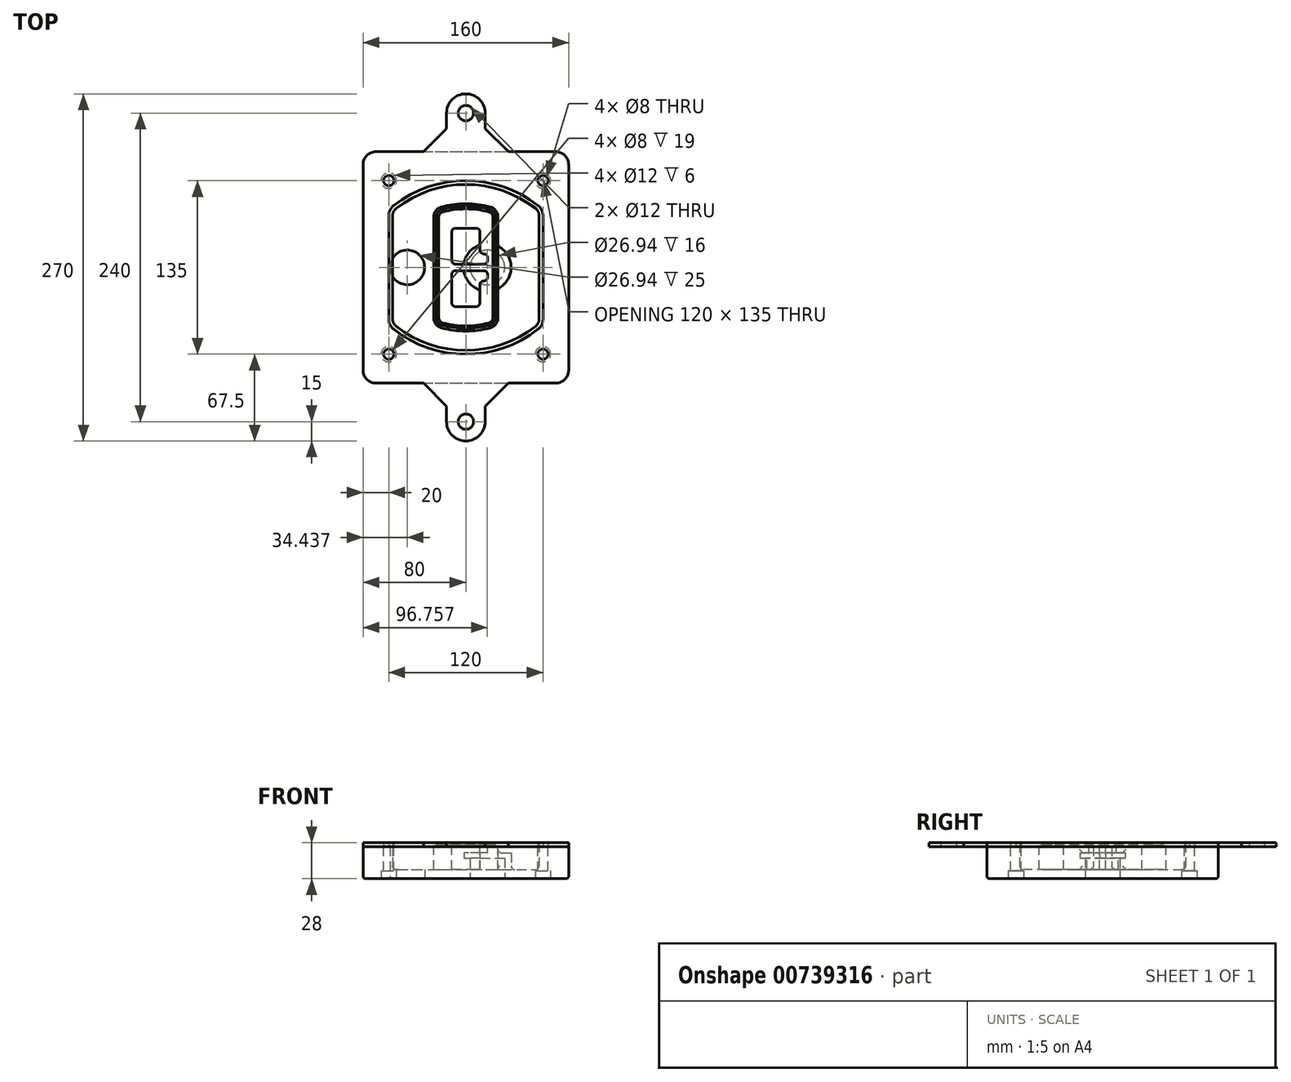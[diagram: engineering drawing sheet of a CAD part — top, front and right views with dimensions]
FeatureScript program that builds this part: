
annotation { "Feature Type Name" : "Feature", "Feature Type Description" : "" }
export const myFeature = defineFeature(function(context is Context, id is Id, definition is map)
    precondition{}
    {
        {
            var Q0;
            Q0=qCreatedBy(makeId("Top.planeOp"),FACE);
            var sketch = newSketch(context, id + "F0", { "sketchPlane" : qUnion([Q0])});
            skPoint(sketch, "E0.rect.middle", {"position": v(0, 0) * mm});
            skLineSegment(sketch, "E1.bottom", {"start": v(-70, -90) * mm, "end": v(70, -90) * mm});
            skLineSegment(sketch, "E1.top", {"start": v(-70, 90) * mm, "end": v(70, 90) * mm});
            skLineSegment(sketch, "E1.left", {"start": v(-80, -80) * mm, "end": v(-80, 80) * mm});
            skLineSegment(sketch, "E1.right", {"start": v(80, -80) * mm, "end": v(80, 80) * mm});
            skLineSegment(sketch, "E2", {"start": v(-80, 90) * mm, "end": v(80, -90) * mm, "construction": true});
            skLineSegment(sketch, "E3", {"start": v(80, 90) * mm, "end": v(-80, -90) * mm, "construction": true});
            skCircle(sketch, "E4", {"center": v(-60, 67.5) * mm, "radius": 4 * mm});
            skCircle(sketch, "E5", {"center": v(60, 67.5) * mm, "radius": 4 * mm});
            skCircle(sketch, "E6", {"center": v(60, -67.5) * mm, "radius": 4 * mm});
            skCircle(sketch, "E7", {"center": v(-60, -67.5) * mm, "radius": 4 * mm});
            skLineSegment(sketch, "E8", {"start": v(-60, 67.5) * mm, "end": v(60, 67.5) * mm, "construction": true});
            skLineSegment(sketch, "E9", {"start": v(60, 67.5) * mm, "end": v(60, -67.5) * mm, "construction": true});
            skLineSegment(sketch, "E10", {"start": v(60, -67.5) * mm, "end": v(-60, -67.5) * mm, "construction": true});
            skLineSegment(sketch, "E11", {"start": v(-60, -67.5) * mm, "end": v(-60, 67.5) * mm, "construction": true});
            skLineSegment(sketch, "E12", {"start": v(-60, 40.3) * mm, "end": v(-60, -40.3) * mm});
            skLineSegment(sketch, "E13", {"start": v(60, 40.3) * mm, "end": v(60, -40.3) * mm});
            skArc(sketch, "E14", {"start": v(56.15, 48.18) * mm, "mid": v(0, 67.5) * mm, "end": v(-56.15, 48.18) * mm});
            skArc(sketch, "E15", {"start": v(-56.15, -48.18) * mm, "mid": v(0, -67.5) * mm, "end": v(56.15, -48.18) * mm});
            skLineSegment(sketch, "E16", {"start": v(-60, 0) * mm, "end": v(60, 0) * mm, "construction": true});
            skPoint(sketch, "E17.visualSharp", {"position": v(-60, -45) * mm});
            skArc(sketch, "E17.filletArc", {"start": v(-60, -40.3) * mm, "mid": v(-58.99, -44.68) * mm, "end": v(-56.15, -48.18) * mm});
            skPoint(sketch, "E18.visualSharp", {"position": v(-60, 45) * mm});
            skArc(sketch, "E18.filletArc", {"start": v(-56.15, 48.18) * mm, "mid": v(-58.99, 44.68) * mm, "end": v(-60, 40.3) * mm});
            skPoint(sketch, "E19.visualSharp", {"position": v(60, 45) * mm});
            skArc(sketch, "E19.filletArc", {"start": v(60, 40.3) * mm, "mid": v(58.99, 44.68) * mm, "end": v(56.15, 48.18) * mm});
            skPoint(sketch, "E20.visualSharp", {"position": v(60, -45) * mm});
            skArc(sketch, "E20.filletArc", {"start": v(56.15, -48.18) * mm, "mid": v(58.99, -44.68) * mm, "end": v(60, -40.3) * mm});
            skPoint(sketch, "E21.visualSharp", {"position": v(-80, 90) * mm});
            skArc(sketch, "E21.filletArc", {"start": v(-70, 90) * mm, "mid": v(-77.07, 87.07) * mm, "end": v(-80, 80) * mm});
            skPoint(sketch, "E22.visualSharp", {"position": v(80, 90) * mm});
            skArc(sketch, "E22.filletArc", {"start": v(80, 80) * mm, "mid": v(77.07, 87.07) * mm, "end": v(70, 90) * mm});
            skPoint(sketch, "E23.visualSharp", {"position": v(80, -90) * mm});
            skArc(sketch, "E23.filletArc", {"start": v(70, -90) * mm, "mid": v(77.07, -87.07) * mm, "end": v(80, -80) * mm});
            skPoint(sketch, "E24.visualSharp", {"position": v(-80, -90) * mm});
            skArc(sketch, "E24.filletArc", {"start": v(-80, -80) * mm, "mid": v(-77.07, -87.07) * mm, "end": v(-70, -90) * mm});
            skArc(sketch, "E25.0", {"start": v(57, 40.3) * mm, "mid": v(56.3, 43.36) * mm, "end": v(54.3, 45.81) * mm});
            skLineSegment(sketch, "E25.1", {"start": v(57, 40.3) * mm, "end": v(57, -40.3) * mm});
            skArc(sketch, "E25.2", {"start": v(54.3, -45.81) * mm, "mid": v(56.3, -43.36) * mm, "end": v(57, -40.3) * mm});
            skArc(sketch, "E25.3", {"start": v(-54.3, -45.81) * mm, "mid": v(0, -64.5) * mm, "end": v(54.3, -45.81) * mm});
            skArc(sketch, "E25.4", {"start": v(-57, -40.3) * mm, "mid": v(-56.3, -43.36) * mm, "end": v(-54.3, -45.81) * mm});
            skArc(sketch, "E25.5", {"start": v(54.3, 45.81) * mm, "mid": v(0, 64.5) * mm, "end": v(-54.3, 45.81) * mm});
            skLineSegment(sketch, "E25.6", {"start": v(-57, 40.3) * mm, "end": v(-57, -40.3) * mm});
            skArc(sketch, "E25.7", {"start": v(-54.3, 45.81) * mm, "mid": v(-56.3, 43.36) * mm, "end": v(-57, 40.3) * mm});
            skArc(sketch, "E26.0", {"start": v(-58.62, 51.33) * mm, "mid": v(-62.58, 46.43) * mm, "end": v(-64, 40.3) * mm});
            skArc(sketch, "E26.1", {"start": v(58.62, 51.33) * mm, "mid": v(0, 71.5) * mm, "end": v(-58.62, 51.33) * mm});
            skArc(sketch, "E26.2", {"start": v(64, 40.3) * mm, "mid": v(62.58, 46.43) * mm, "end": v(58.62, 51.33) * mm});
            skLineSegment(sketch, "E26.3", {"start": v(64, 40.3) * mm, "end": v(64, -40.3) * mm});
            skArc(sketch, "E26.4", {"start": v(58.62, -51.33) * mm, "mid": v(62.58, -46.43) * mm, "end": v(64, -40.3) * mm});
            skLineSegment(sketch, "E26.5", {"start": v(-64, 40.3) * mm, "end": v(-64, -40.3) * mm});
            skArc(sketch, "E26.6", {"start": v(-58.62, -51.33) * mm, "mid": v(0, -71.5) * mm, "end": v(58.62, -51.33) * mm});
            skArc(sketch, "E26.7", {"start": v(-64, -40.3) * mm, "mid": v(-62.58, -46.43) * mm, "end": v(-58.62, -51.33) * mm});
            skSolve(sketch);
        }
        {
            var Q0;
            Q0=makeQuery(id+"F0.imprint","IMPRINT",FACE,{"disambiguationData":[TD([[makeQuery(id+"F0.imprint","IMPRINT",EDGE,{"derivedFrom":sQuery(id+"F0.wireOp",EDGE,"E1.bottom")}),1.0]])]});
            var Q1;
            Q1=makeQuery(id+"F0.imprint","IMPRINT",FACE,{"disambiguationData":[TD([[makeQuery(id+"F0.imprint","IMPRINT",EDGE,{"derivedFrom":sQuery(id+"F0.wireOp",EDGE,"E12")}),1.0]])]});
            var Q2;
            Q2=makeQuery(id+"F0.imprint","IMPRINT",FACE,{"disambiguationData":[TD([[makeQuery(id+"F0.imprint","IMPRINT",EDGE,{"derivedFrom":sQuery(id+"F0.wireOp",EDGE,"E25.0")}),1.0]])]});
            var Q3;
            Q3=makeQuery(id+"F0.imprint","IMPRINT",FACE,{"disambiguationData":[TD([[makeQuery(id+"F0.imprint","IMPRINT",EDGE,{"derivedFrom":sQuery(id+"F0.wireOp",EDGE,"E12")}),-1.0]])]});
            extrude(context, id + "F1", {"entities" : qUnion([Q0, Q1, Q2, Q3]), "oppositeDirection" : true, "depth" : 25 * mm});
        }
        {
            var Q0;
            Q0=makeQuery(id+"F0.imprint","IMPRINT",FACE,{"disambiguationData":[TD([[makeQuery(id+"F0.imprint","IMPRINT",EDGE,{"derivedFrom":sQuery(id+"F0.wireOp",EDGE,"E12")}),1.0]])]});
            extrude(context, id + "F2", {"entities" : qUnion([Q0]), "operationType" : NewBodyOperationType.ADD, "depth" : 3 * mm, "offsetDistance" : 25 * mm});
        }
        {
            var Q0;
            Q0=makeQuery(id+"F0.imprint","IMPRINT",FACE,{"disambiguationData":[TD([[makeQuery(id+"F0.imprint","IMPRINT",EDGE,{"derivedFrom":sQuery(id+"F0.wireOp",EDGE,"E25.0")}),1.0]])]});
            extrude(context, id + "F3", {"entities" : qUnion([Q0]), "operationType" : NewBodyOperationType.REMOVE, "oppositeDirection" : true, "depth" : 18 * mm});
        }
        {
            var Q0;
            Q0=makeQuery(id+"F2.opExtrude","CAP_FACE",FACE,{"disambiguationData":[OSD([sQuery(id+"F0.wireOp",EDGE,"E12"),sQuery(id+"F0.wireOp",EDGE,"E13"),sQuery(id+"F0.wireOp",EDGE,"E14"),sQuery(id+"F0.wireOp",EDGE,"E15"),sQuery(id+"F0.wireOp",EDGE,"E17.filletArc"),sQuery(id+"F0.wireOp",EDGE,"E18.filletArc"),sQuery(id+"F0.wireOp",EDGE,"E19.filletArc"),sQuery(id+"F0.wireOp",EDGE,"E20.filletArc"),sQuery(id+"F0.wireOp",EDGE,"E25.0"),sQuery(id+"F0.wireOp",EDGE,"E25.1"),sQuery(id+"F0.wireOp",EDGE,"E25.2"),sQuery(id+"F0.wireOp",EDGE,"E25.3"),sQuery(id+"F0.wireOp",EDGE,"E25.4"),sQuery(id+"F0.wireOp",EDGE,"E25.5"),sQuery(id+"F0.wireOp",EDGE,"E25.6"),sQuery(id+"F0.wireOp",EDGE,"E25.7")])],"isStart":false});
            var sketch = newSketch(context, id + "F4", { "sketchPlane" : qUnion([Q0])});
            skArc(sketch, "E27.0", {"start": v(-19.08, -46.97) * mm, "mid": v(0, -49.5) * mm, "end": v(19.08, -46.97) * mm});
            skArc(sketch, "E28.0", {"start": v(19.08, 46.97) * mm, "mid": v(0, 49.5) * mm, "end": v(-19.08, 46.97) * mm});
            skLineSegment(sketch, "E29", {"start": v(-25, 39.25) * mm, "end": v(-25, -39.25) * mm});
            skLineSegment(sketch, "E30", {"start": v(25, 39.25) * mm, "end": v(25, -39.25) * mm});
            skLineSegment(sketch, "E31", {"start": v(-25, 45.1) * mm, "end": v(25, 45.1) * mm, "construction": true});
            skLineSegment(sketch, "E32", {"start": v(-25, -45.1) * mm, "end": v(25, -45.1) * mm, "construction": true});
            skPoint(sketch, "E33.visualSharp", {"position": v(-25, 45.1) * mm});
            skArc(sketch, "E33.filletArc", {"start": v(-19.08, 46.97) * mm, "mid": v(-23.35, 44.11) * mm, "end": v(-25, 39.25) * mm});
            skPoint(sketch, "E34.visualSharp", {"position": v(25, 45.1) * mm});
            skArc(sketch, "E34.filletArc", {"start": v(25, 39.25) * mm, "mid": v(23.35, 44.11) * mm, "end": v(19.08, 46.97) * mm});
            skPoint(sketch, "E35.visualSharp", {"position": v(25, -45.1) * mm});
            skArc(sketch, "E35.filletArc", {"start": v(19.08, -46.97) * mm, "mid": v(23.35, -44.11) * mm, "end": v(25, -39.25) * mm});
            skPoint(sketch, "E36.visualSharp", {"position": v(-25, -45.1) * mm});
            skArc(sketch, "E36.filletArc", {"start": v(-25, -39.25) * mm, "mid": v(-23.35, -44.11) * mm, "end": v(-19.08, -46.97) * mm});
            skArc(sketch, "E37.0", {"start": v(54.3, 45.81) * mm, "mid": v(0, 64.5) * mm, "end": v(-54.3, 45.81) * mm});
            skArc(sketch, "E37.1", {"start": v(-54.3, 45.81) * mm, "mid": v(-56.3, 43.36) * mm, "end": v(-57, 40.3) * mm});
            skLineSegment(sketch, "E37.2", {"start": v(-57, 40.3) * mm, "end": v(-57, -40.3) * mm});
            skArc(sketch, "E37.3", {"start": v(-57, -40.3) * mm, "mid": v(-56.3, -43.36) * mm, "end": v(-54.3, -45.81) * mm});
            skArc(sketch, "E37.4", {"start": v(-54.3, -45.81) * mm, "mid": v(0, -64.5) * mm, "end": v(54.3, -45.81) * mm});
            skArc(sketch, "E37.5", {"start": v(54.3, -45.81) * mm, "mid": v(56.3, -43.36) * mm, "end": v(57, -40.3) * mm});
            skLineSegment(sketch, "E37.6", {"start": v(57, 40.3) * mm, "end": v(57, -40.3) * mm});
            skArc(sketch, "E37.7", {"start": v(57, 40.3) * mm, "mid": v(56.3, 43.36) * mm, "end": v(54.3, 45.81) * mm});
            skLineSegment(sketch, "E38.0", {"start": v(23, 39.25) * mm, "end": v(23, -39.25) * mm});
            skArc(sketch, "E38.1", {"start": v(18.56, -45.04) * mm, "mid": v(21.76, -42.9) * mm, "end": v(23, -39.25) * mm});
            skArc(sketch, "E38.2", {"start": v(-18.56, -45.04) * mm, "mid": v(0, -47.5) * mm, "end": v(18.56, -45.04) * mm});
            skArc(sketch, "E38.3", {"start": v(-23, -39.25) * mm, "mid": v(-21.76, -42.9) * mm, "end": v(-18.56, -45.04) * mm});
            skLineSegment(sketch, "E38.4", {"start": v(-23, 39.25) * mm, "end": v(-23, -39.25) * mm});
            skArc(sketch, "E38.5", {"start": v(23, 39.25) * mm, "mid": v(21.76, 42.9) * mm, "end": v(18.56, 45.04) * mm});
            skArc(sketch, "E38.6", {"start": v(-18.56, 45.04) * mm, "mid": v(-21.76, 42.9) * mm, "end": v(-23, 39.25) * mm});
            skArc(sketch, "E38.7", {"start": v(18.56, 45.04) * mm, "mid": v(0, 47.5) * mm, "end": v(-18.56, 45.04) * mm});
            skArc(sketch, "E39.0", {"start": v(21, 39.25) * mm, "mid": v(20.18, 41.68) * mm, "end": v(18.04, 43.1) * mm});
            skLineSegment(sketch, "E39.1", {"start": v(21, 39.25) * mm, "end": v(21, -39.25) * mm});
            skArc(sketch, "E39.2", {"start": v(18.04, -43.1) * mm, "mid": v(20.18, -41.68) * mm, "end": v(21, -39.25) * mm});
            skArc(sketch, "E39.3", {"start": v(-18.04, -43.1) * mm, "mid": v(0, -45.5) * mm, "end": v(18.04, -43.1) * mm});
            skArc(sketch, "E39.4", {"start": v(-21, -39.25) * mm, "mid": v(-20.18, -41.68) * mm, "end": v(-18.04, -43.1) * mm});
            skArc(sketch, "E39.5", {"start": v(18.04, 43.1) * mm, "mid": v(0, 45.5) * mm, "end": v(-18.04, 43.1) * mm});
            skLineSegment(sketch, "E39.6", {"start": v(-21, 39.25) * mm, "end": v(-21, -39.25) * mm});
            skArc(sketch, "E39.7", {"start": v(-18.04, 43.1) * mm, "mid": v(-20.18, 41.68) * mm, "end": v(-21, 39.25) * mm});
            skLineSegment(sketch, "E40", {"start": v(-25, 0) * mm, "end": v(25, 0) * mm, "construction": true});
            skLineSegment(sketch, "E41", {"start": v(-11, 5.5) * mm, "end": v(-11, 27.5) * mm});
            skLineSegment(sketch, "E42", {"start": v(-8, 30.5) * mm, "end": v(8, 30.5) * mm});
            skLineSegment(sketch, "E43", {"start": v(11, 27.5) * mm, "end": v(11, 13.5) * mm});
            skLineSegment(sketch, "E44", {"start": v(14, 10.5) * mm, "end": v(14, 10.5) * mm});
            skLineSegment(sketch, "E45", {"start": v(17, 7.5) * mm, "end": v(17, 5.5) * mm});
            skLineSegment(sketch, "E46", {"start": v(14, 2.5) * mm, "end": v(-8, 2.5) * mm});
            skPoint(sketch, "E47.visualSharp", {"position": v(-11, 30.5) * mm});
            skArc(sketch, "E47.filletArc", {"start": v(-8, 30.5) * mm, "mid": v(-10.12, 29.62) * mm, "end": v(-11, 27.5) * mm});
            skPoint(sketch, "E48.visualSharp", {"position": v(11, 30.5) * mm});
            skArc(sketch, "E48.filletArc", {"start": v(11, 27.5) * mm, "mid": v(10.12, 29.62) * mm, "end": v(8, 30.5) * mm});
            skPoint(sketch, "E49.visualSharp", {"position": v(11, 10.5) * mm});
            skArc(sketch, "E49.filletArc", {"start": v(11, 13.5) * mm, "mid": v(11.88, 11.38) * mm, "end": v(14, 10.5) * mm});
            skPoint(sketch, "E50.visualSharp", {"position": v(17, 10.5) * mm});
            skArc(sketch, "E50.filletArc", {"start": v(17, 7.5) * mm, "mid": v(16.12, 9.62) * mm, "end": v(14, 10.5) * mm});
            skPoint(sketch, "E51.visualSharp", {"position": v(17, 2.5) * mm});
            skArc(sketch, "E51.filletArc", {"start": v(14, 2.5) * mm, "mid": v(16.12, 3.38) * mm, "end": v(17, 5.5) * mm});
            skPoint(sketch, "E52.visualSharp", {"position": v(-11, 2.5) * mm});
            skArc(sketch, "E52.filletArc", {"start": v(-11, 5.5) * mm, "mid": v(-10.12, 3.38) * mm, "end": v(-8, 2.5) * mm});
            skLineSegment(sketch, "E53.0.MirrorCS", {"start": v(14, -2.5) * mm, "end": v(-8, -2.5) * mm});
            skArc(sketch, "E54.0.MirrorCS", {"start": v(-11, -5.5) * mm, "mid": v(-10.12, -3.38) * mm, "end": v(-8, -2.5) * mm});
            skLineSegment(sketch, "E55.0.MirrorCS", {"start": v(-11, -5.5) * mm, "end": v(-11, -27.5) * mm});
            skArc(sketch, "E56.0.MirrorCS", {"start": v(-8, -30.5) * mm, "mid": v(-10.12, -29.62) * mm, "end": v(-11, -27.5) * mm});
            skLineSegment(sketch, "E57.0.MirrorCS", {"start": v(-8, -30.5) * mm, "end": v(8, -30.5) * mm});
            skArc(sketch, "E58.0.MirrorCS", {"start": v(11, -27.5) * mm, "mid": v(10.12, -29.62) * mm, "end": v(8, -30.5) * mm});
            skLineSegment(sketch, "E59.0.MirrorCS", {"start": v(11, -27.5) * mm, "end": v(11, -13.5) * mm});
            skArc(sketch, "E60.0.MirrorCS", {"start": v(11, -13.5) * mm, "mid": v(11.88, -11.38) * mm, "end": v(14, -10.5) * mm});
            skArc(sketch, "E61.0.MirrorCS", {"start": v(17, -7.5) * mm, "mid": v(16.12, -9.62) * mm, "end": v(14, -10.5) * mm});
            skLineSegment(sketch, "E62.0.MirrorCS", {"start": v(17, -7.5) * mm, "end": v(17, -5.5) * mm});
            skArc(sketch, "E63.0.MirrorCS", {"start": v(14, -2.5) * mm, "mid": v(16.12, -3.38) * mm, "end": v(17, -5.5) * mm});
            skSolve(sketch);
        }
        {
            var Q0;
            Q0=makeQuery(id+"F4.imprint","IMPRINT",FACE,{"disambiguationData":[TD([[makeQuery(id+"F4.imprint","IMPRINT",EDGE,{"derivedFrom":sQuery(id+"F4.wireOp",EDGE,"E27.0")}),1.0]])]});
            var Q1;
            Q1=makeQuery(id+"F4.imprint","IMPRINT",FACE,{"disambiguationData":[TD([[makeQuery(id+"F4.imprint","IMPRINT",EDGE,{"derivedFrom":sQuery(id+"F4.wireOp",EDGE,"E38.0")}),-1.0]])]});
            var Q2;
            Q2=makeQuery(id+"F4.imprint","IMPRINT",FACE,{"disambiguationData":[TD([[makeQuery(id+"F4.imprint","IMPRINT",EDGE,{"derivedFrom":sQuery(id+"F4.wireOp",EDGE,"E39.0")}),1.0]])]});
            extrude(context, id + "F5", {"entities" : qUnion([Q0, Q1, Q2]), "operationType" : NewBodyOperationType.ADD, "endBound" : BoundingType.UP_TO_NEXT, "oppositeDirection" : true, "depth" : 25 * mm});
        }
        {
            var Q0;
            Q0=makeQuery(id+"F4.imprint","IMPRINT",FACE,{"disambiguationData":[TD([[makeQuery(id+"F4.imprint","IMPRINT",EDGE,{"derivedFrom":sQuery(id+"F4.wireOp",EDGE,"E38.0")}),-1.0]])]});
            extrude(context, id + "F6", {"entities" : qUnion([Q0]), "operationType" : NewBodyOperationType.REMOVE, "oppositeDirection" : true, "depth" : 2 * mm});
        }
        {
            var Q0;
            Q0=makeQuery(id+"F1.opExtrude","CAP_FACE",FACE,{"disambiguationData":[OSD([sQuery(id+"F0.wireOp",EDGE,"E1.bottom"),sQuery(id+"F0.wireOp",EDGE,"E1.top"),sQuery(id+"F0.wireOp",EDGE,"E1.left"),sQuery(id+"F0.wireOp",EDGE,"E1.right"),sQuery(id+"F0.wireOp",EDGE,"E4"),sQuery(id+"F0.wireOp",EDGE,"E5"),sQuery(id+"F0.wireOp",EDGE,"E6"),sQuery(id+"F0.wireOp",EDGE,"E7"),sQuery(id+"F0.wireOp",EDGE,"E21.filletArc"),sQuery(id+"F0.wireOp",EDGE,"E22.filletArc"),sQuery(id+"F0.wireOp",EDGE,"E23.filletArc"),sQuery(id+"F0.wireOp",EDGE,"E24.filletArc")])],"isStart":false});
            var sketch = newSketch(context, id + "F7", { "sketchPlane" : qUnion([Q0])});
            skCircle(sketch, "E64", {"center": v(16.76, 0) * mm, "radius": 13.47 * mm});
            skCircle(sketch, "E65", {"center": v(-45.56, 0) * mm, "radius": 13.47 * mm});
            skLineSegment(sketch, "E66", {"start": v(80, 0) * mm, "end": v(-80, 0) * mm});
            skCircle(sketch, "E67", {"center": v(16.76, 0) * mm, "radius": 18.47 * mm});
            skCircle(sketch, "E68", {"center": v(60, -67.5) * mm, "radius": 6 * mm});
            skCircle(sketch, "E69", {"center": v(-60, -67.5) * mm, "radius": 6 * mm});
            skCircle(sketch, "E70", {"center": v(-60, 67.5) * mm, "radius": 6 * mm});
            skCircle(sketch, "E71", {"center": v(60, 67.5) * mm, "radius": 6 * mm});
            skSolve(sketch);
        }
        {
            var Q0;
            {var subQ1=sQuery(id+"F7.wireOp",EDGE,"E66");var subQ4=sQuery(id+"F7.wireOp",EDGE,"E64");var subQ6=makeQuery(id+"F7.imprint","INTERSECT",VERTEX,{"disambiguationData":[OD(0.0)],"derivedFrom":[subQ4,subQ1]});Q0=makeQuery(id+"F7.imprint","IMPRINT",FACE,{"disambiguationData":[TD([[makeQuery(id+"F7.imprint","IMPRINT",EDGE,{"disambiguationData":[TD([[subQ6,-1.0]])],"derivedFrom":subQ4}),-1.0]])]});}
            var Q1;
            {var subQ0=sQuery(id+"F7.wireOp",EDGE,"E66");var subQ1=sQuery(id+"F7.wireOp",EDGE,"E64");var subQ3=makeQuery(id+"F7.imprint","INTERSECT",VERTEX,{"disambiguationData":[OD(0.0)],"derivedFrom":[subQ1,subQ0]});Q1=makeQuery(id+"F7.imprint","IMPRINT",FACE,{"disambiguationData":[TD([[makeQuery(id+"F7.imprint","IMPRINT",EDGE,{"disambiguationData":[TD([[subQ3,-1.0]])],"derivedFrom":subQ1}),1.0]])]});}
            var Q2;
            {var subQ0=sQuery(id+"F7.wireOp",EDGE,"E66");var subQ1=sQuery(id+"F7.wireOp",EDGE,"E64");var subQ3=makeQuery(id+"F7.imprint","INTERSECT",VERTEX,{"disambiguationData":[OD(0.0)],"derivedFrom":[subQ1,subQ0]});Q2=makeQuery(id+"F7.imprint","IMPRINT",FACE,{"disambiguationData":[TD([[makeQuery(id+"F7.imprint","IMPRINT",EDGE,{"disambiguationData":[TD([[subQ3,1.0]])],"derivedFrom":subQ1}),1.0]])]});}
            var Q3;
            {var subQ1=sQuery(id+"F7.wireOp",EDGE,"E66");var subQ4=sQuery(id+"F7.wireOp",EDGE,"E64");var subQ6=makeQuery(id+"F7.imprint","INTERSECT",VERTEX,{"disambiguationData":[OD(0.0)],"derivedFrom":[subQ4,subQ1]});Q3=makeQuery(id+"F7.imprint","IMPRINT",FACE,{"disambiguationData":[TD([[makeQuery(id+"F7.imprint","IMPRINT",EDGE,{"disambiguationData":[TD([[subQ6,1.0]])],"derivedFrom":subQ4}),-1.0]])]});}
            extrude(context, id + "F8", {"entities" : qUnion([Q0, Q1, Q2, Q3]), "operationType" : NewBodyOperationType.ADD, "oppositeDirection" : true, "depth" : 20 * mm});
        }
        {
            var Q0;
            {var subQ0=sQuery(id+"F7.wireOp",EDGE,"E66");var subQ1=sQuery(id+"F7.wireOp",EDGE,"E64");var subQ3=makeQuery(id+"F7.imprint","INTERSECT",VERTEX,{"disambiguationData":[OD(0.0)],"derivedFrom":[subQ1,subQ0]});Q0=makeQuery(id+"F7.imprint","IMPRINT",FACE,{"disambiguationData":[TD([[makeQuery(id+"F7.imprint","IMPRINT",EDGE,{"disambiguationData":[TD([[subQ3,-1.0]])],"derivedFrom":subQ1}),1.0]])]});}
            var Q1;
            {var subQ0=sQuery(id+"F7.wireOp",EDGE,"E66");var subQ1=sQuery(id+"F7.wireOp",EDGE,"E64");var subQ3=makeQuery(id+"F7.imprint","INTERSECT",VERTEX,{"disambiguationData":[OD(0.0)],"derivedFrom":[subQ1,subQ0]});Q1=makeQuery(id+"F7.imprint","IMPRINT",FACE,{"disambiguationData":[TD([[makeQuery(id+"F7.imprint","IMPRINT",EDGE,{"disambiguationData":[TD([[subQ3,1.0]])],"derivedFrom":subQ1}),1.0]])]});}
            extrude(context, id + "F9", {"entities" : qUnion([Q0, Q1]), "operationType" : NewBodyOperationType.REMOVE, "oppositeDirection" : true, "depth" : 16 * mm});
        }
        {
            var Q0;
            {var subQ0=sQuery(id+"F7.wireOp",EDGE,"E66");var subQ1=sQuery(id+"F7.wireOp",EDGE,"E65");var subQ3=makeQuery(id+"F7.imprint","INTERSECT",VERTEX,{"disambiguationData":[OD(0.0)],"derivedFrom":[subQ1,subQ0]});Q0=makeQuery(id+"F7.imprint","IMPRINT",FACE,{"disambiguationData":[TD([[makeQuery(id+"F7.imprint","IMPRINT",EDGE,{"disambiguationData":[TD([[subQ3,-1.0]])],"derivedFrom":subQ1}),1.0]])]});}
            var Q1;
            {var subQ0=sQuery(id+"F7.wireOp",EDGE,"E66");var subQ1=sQuery(id+"F7.wireOp",EDGE,"E65");var subQ3=makeQuery(id+"F7.imprint","INTERSECT",VERTEX,{"disambiguationData":[OD(0.0)],"derivedFrom":[subQ1,subQ0]});Q1=makeQuery(id+"F7.imprint","IMPRINT",FACE,{"disambiguationData":[TD([[makeQuery(id+"F7.imprint","IMPRINT",EDGE,{"disambiguationData":[TD([[subQ3,1.0]])],"derivedFrom":subQ1}),1.0]])]});}
            extrude(context, id + "F10", {"entities" : qUnion([Q0, Q1]), "operationType" : NewBodyOperationType.REMOVE, "oppositeDirection" : true, "depth" : 25 * mm});
        }
        {
            var Q0;
            Q0=makeQuery(id+"F7.imprint","IMPRINT",FACE,{"disambiguationData":[TD([[makeQuery(id+"F7.imprint","IMPRINT",EDGE,{"derivedFrom":sQuery(id+"F7.wireOp",EDGE,"E68")}),1.0]])]});
            var Q1;
            Q1=makeQuery(id+"F7.imprint","IMPRINT",FACE,{"disambiguationData":[TD([[makeQuery(id+"F7.imprint","IMPRINT",EDGE,{"derivedFrom":makeQuery(id+"F1.opExtrude","CAP_EDGE",EDGE,{"disambiguationData":[OSD([sQuery(id+"F0.wireOp",EDGE,"E5")])],"isStart":false})}),-1.0]])]});
            var Q2;
            Q2=makeQuery(id+"F7.imprint","IMPRINT",FACE,{"disambiguationData":[TD([[makeQuery(id+"F7.imprint","IMPRINT",EDGE,{"derivedFrom":sQuery(id+"F7.wireOp",EDGE,"E69")}),1.0]])]});
            var Q3;
            Q3=makeQuery(id+"F7.imprint","IMPRINT",FACE,{"disambiguationData":[TD([[makeQuery(id+"F7.imprint","IMPRINT",EDGE,{"derivedFrom":makeQuery(id+"F1.opExtrude","CAP_EDGE",EDGE,{"disambiguationData":[OSD([sQuery(id+"F0.wireOp",EDGE,"E4")])],"isStart":false})}),-1.0]])]});
            var Q4;
            Q4=makeQuery(id+"F7.imprint","IMPRINT",FACE,{"disambiguationData":[TD([[makeQuery(id+"F7.imprint","IMPRINT",EDGE,{"derivedFrom":sQuery(id+"F7.wireOp",EDGE,"E70")}),1.0]])]});
            var Q5;
            Q5=makeQuery(id+"F7.imprint","IMPRINT",FACE,{"disambiguationData":[TD([[makeQuery(id+"F7.imprint","IMPRINT",EDGE,{"derivedFrom":makeQuery(id+"F1.opExtrude","CAP_EDGE",EDGE,{"disambiguationData":[OSD([sQuery(id+"F0.wireOp",EDGE,"E7")])],"isStart":false})}),-1.0]])]});
            var Q6;
            Q6=makeQuery(id+"F7.imprint","IMPRINT",FACE,{"disambiguationData":[TD([[makeQuery(id+"F7.imprint","IMPRINT",EDGE,{"derivedFrom":sQuery(id+"F7.wireOp",EDGE,"E71")}),1.0]])]});
            var Q7;
            Q7=makeQuery(id+"F7.imprint","IMPRINT",FACE,{"disambiguationData":[TD([[makeQuery(id+"F7.imprint","IMPRINT",EDGE,{"derivedFrom":makeQuery(id+"F1.opExtrude","CAP_EDGE",EDGE,{"disambiguationData":[OSD([sQuery(id+"F0.wireOp",EDGE,"E6")])],"isStart":false})}),-1.0]])]});
            extrude(context, id + "F11", {"entities" : qUnion([Q0, Q1, Q2, Q3, Q4, Q5, Q6, Q7]), "operationType" : NewBodyOperationType.REMOVE, "oppositeDirection" : true, "depth" : 6 * mm});
        }
        {
            var Q0;
            Q0=makeQuery(id+"F9.boolean.opBoolean","COPY",FACE,{"derivedFrom":makeQuery(id+"F9.opExtrude","CAP_FACE",FACE,{"disambiguationData":[OSD([sQuery(id+"F7.wireOp",EDGE,"E64")])],"isStart":false})});
            var sketch = newSketch(context, id + "F12", { "sketchPlane" : qUnion([Q0])});
            skArc(sketch, "E72.0", {"start": v(11, 17.55) * mm, "mid": v(2.57, 11.82) * mm, "end": v(-1.54, 2.5) * mm});
            skArc(sketch, "E72.1", {"start": v(-1.54, -2.5) * mm, "mid": v(2.57, -11.82) * mm, "end": v(11, -17.55) * mm});
            skLineSegment(sketch, "E73", {"start": v(-1.54, -2.5) * mm, "end": v(14, -2.5) * mm});
            skLineSegment(sketch, "E74.0", {"start": v(14, 2.5) * mm, "end": v(-1.54, 2.5) * mm});
            skArc(sketch, "E74.1", {"start": v(14, 2.5) * mm, "mid": v(16.12, 3.38) * mm, "end": v(17, 5.5) * mm});
            skLineSegment(sketch, "E74.2", {"start": v(17, 7.5) * mm, "end": v(17, 5.5) * mm});
            skArc(sketch, "E74.3", {"start": v(17, 7.5) * mm, "mid": v(16.12, 9.62) * mm, "end": v(14, 10.5) * mm});
            skArc(sketch, "E74.4", {"start": v(11, 13.5) * mm, "mid": v(11.88, 11.38) * mm, "end": v(14, 10.5) * mm});
            skLineSegment(sketch, "E74.5", {"start": v(11, 17.55) * mm, "end": v(11, 13.5) * mm});
            skLineSegment(sketch, "E74.7", {"start": v(14, -2.5) * mm, "end": v(-1.54, -2.5) * mm});
            skArc(sketch, "E74.8", {"start": v(14, -2.5) * mm, "mid": v(16.12, -3.38) * mm, "end": v(17, -5.5) * mm});
            skLineSegment(sketch, "E74.9", {"start": v(17, -7.5) * mm, "end": v(17, -5.5) * mm});
            skArc(sketch, "E74.10", {"start": v(17, -7.5) * mm, "mid": v(16.12, -9.62) * mm, "end": v(14, -10.5) * mm});
            skArc(sketch, "E74.11", {"start": v(11, -13.5) * mm, "mid": v(11.88, -11.38) * mm, "end": v(14, -10.5) * mm});
            skLineSegment(sketch, "E74.12", {"start": v(11, -17.55) * mm, "end": v(11, -13.5) * mm});
            skPoint(sketch, "E75.orphan", {"position": v(11, -27.5) * mm});
            skPoint(sketch, "E76.orphan", {"position": v(-8, -2.5) * mm});
            skPoint(sketch, "E77.orphan", {"position": v(-8, 2.5) * mm});
            skPoint(sketch, "E78.orphan", {"position": v(11, 27.5) * mm});
            skSolve(sketch);
        }
        {
            var Q0;
            {var subQ7=sQuery(id+"F12.wireOp",EDGE,"E72.0");var subQ14=sQuery(id+"F12.wireOp",EDGE,"E72.1");var subQ16=sQuery(id+"F12.wireOp",EDGE,"E74.1");var subQ18=sQuery(id+"F12.wireOp",EDGE,"E74.8");Q0=qUnion([makeQuery(id+"F12.imprint","IMPRINT",FACE,{"disambiguationData":[TD([[makeQuery(id+"F12.imprint","IMPRINT",EDGE,{"derivedFrom":subQ7}),1.0]])]}),makeQuery(id+"F12.imprint","IMPRINT",FACE,{"disambiguationData":[TD([[makeQuery(id+"F12.imprint","IMPRINT",EDGE,{"derivedFrom":subQ14}),1.0]])]}),makeQuery(id+"F12.imprint","IMPRINT",FACE,{"disambiguationData":[TD([[makeQuery(id+"F12.imprint","IMPRINT",EDGE,{"derivedFrom":subQ16}),1.0]])]}),makeQuery(id+"F12.imprint","IMPRINT",FACE,{"disambiguationData":[TD([[makeQuery(id+"F12.imprint","IMPRINT",EDGE,{"derivedFrom":subQ18}),-1.0]])]})]);}
            var Q1;
            Q1=makeQuery(id+"F5.boolean.opBoolean","SPLIT",FACE,{"disambiguationData":[TD([makeQuery(id+"F5.opExtrude","SWEPT_FACE",FACE,{"disambiguationData":[OSD([sQuery(id+"F4.wireOp",EDGE,"E41")])]})])],"derivedFrom":makeQuery(id+"F3.boolean.opBoolean","COPY",FACE,{"derivedFrom":makeQuery(id+"F3.opExtrude","CAP_FACE",FACE,{"disambiguationData":[OSD([sQuery(id+"F0.wireOp",EDGE,"E25.0"),sQuery(id+"F0.wireOp",EDGE,"E25.1"),sQuery(id+"F0.wireOp",EDGE,"E25.2"),sQuery(id+"F0.wireOp",EDGE,"E25.3"),sQuery(id+"F0.wireOp",EDGE,"E25.4"),sQuery(id+"F0.wireOp",EDGE,"E25.5"),sQuery(id+"F0.wireOp",EDGE,"E25.6"),sQuery(id+"F0.wireOp",EDGE,"E25.7")])],"isStart":false})})});
            extrude(context, id + "F13", {"entities" : qUnion([Q0]), "operationType" : NewBodyOperationType.REMOVE, "endBound" : BoundingType.UP_TO_SURFACE, "endBoundEntityFace" : qUnion([Q1]), "depth" : 25 * mm});
        }
        {
            var Q0;
            Q0=makeQuery(id+"F3.boolean.opBoolean","COPY",EDGE,{"derivedFrom":makeQuery(id+"F3.opExtrude","CAP_EDGE",EDGE,{"disambiguationData":[OSD([sQuery(id+"F0.wireOp",EDGE,"E25.6")])],"isStart":false})});
            var Q1;
            Q1=makeQuery(id+"F8.boolean.opBoolean","INTERSECT",EDGE,{"derivedFrom":[makeQuery(id+"F5.opExtrude","SWEPT_FACE",FACE,{"disambiguationData":[OSD([sQuery(id+"F4.wireOp",EDGE,"E30")])]}),makeQuery(id+"F8.opExtrude","CAP_FACE",FACE,{"disambiguationData":[OSD([sQuery(id+"F7.wireOp",EDGE,"E67")])],"isStart":false})]});
            var Q2;
            Q2=makeQuery(id+"F8.boolean.opBoolean","INTERSECT",EDGE,{"disambiguationData":[OD(1.0)],"derivedFrom":[makeQuery(id+"F5.opExtrude","SWEPT_FACE",FACE,{"disambiguationData":[OSD([sQuery(id+"F4.wireOp",EDGE,"E30")])]}),makeQuery(id+"F8.opExtrude","SWEPT_FACE",FACE,{"disambiguationData":[OSD([sQuery(id+"F7.wireOp",EDGE,"E67")])]})]});
            var Q3;
            {var subQ0=makeQuery(id+"F3.boolean.opBoolean","COPY",FACE,{"derivedFrom":makeQuery(id+"F3.opExtrude","CAP_FACE",FACE,{"disambiguationData":[OSD([sQuery(id+"F0.wireOp",EDGE,"E25.0"),sQuery(id+"F0.wireOp",EDGE,"E25.1"),sQuery(id+"F0.wireOp",EDGE,"E25.2"),sQuery(id+"F0.wireOp",EDGE,"E25.3"),sQuery(id+"F0.wireOp",EDGE,"E25.4"),sQuery(id+"F0.wireOp",EDGE,"E25.5"),sQuery(id+"F0.wireOp",EDGE,"E25.6"),sQuery(id+"F0.wireOp",EDGE,"E25.7")])],"isStart":false})});var subQ1=sQuery(id+"F4.wireOp",EDGE,"E30");Q3=makeQuery(id+"F8.boolean.opBoolean","SPLIT",EDGE,{"disambiguationData":[TD([makeQuery(id+"F5.opExtrude","SWEPT_FACE",FACE,{"disambiguationData":[OSD([sQuery(id+"F4.wireOp",EDGE,"E35.filletArc")])]})])],"derivedFrom":makeQuery(id+"F5.opExtrude","TWEAK_EDGE",EDGE,{"derivedFrom":[subQ0,makeQuery(id+"F4.imprint","IMPRINT",EDGE,{"derivedFrom":subQ1})]})});}
            var Q4;
            {var subQ0=sQuery(id+"F0.wireOp",EDGE,"E25.0");var subQ1=sQuery(id+"F0.wireOp",EDGE,"E25.1");var subQ2=sQuery(id+"F0.wireOp",EDGE,"E25.2");var subQ3=sQuery(id+"F0.wireOp",EDGE,"E25.3");var subQ4=sQuery(id+"F0.wireOp",EDGE,"E25.4");var subQ5=sQuery(id+"F0.wireOp",EDGE,"E25.5");var subQ6=sQuery(id+"F0.wireOp",EDGE,"E25.6");var subQ7=sQuery(id+"F0.wireOp",EDGE,"E25.7");Q4=makeQuery(id+"F8.boolean.opBoolean","INTERSECT",EDGE,{"derivedFrom":[makeQuery(id+"F5.boolean.opBoolean","SPLIT",FACE,{"disambiguationData":[TD([makeQuery(id+"F2.opExtrude","SWEPT_FACE",FACE,{"disambiguationData":[OSD([subQ0])]})])],"derivedFrom":makeQuery(id+"F3.boolean.opBoolean","COPY",FACE,{"derivedFrom":makeQuery(id+"F3.opExtrude","CAP_FACE",FACE,{"disambiguationData":[OSD([subQ0,subQ1,subQ2,subQ3,subQ4,subQ5,subQ6,subQ7])],"isStart":false})})}),makeQuery(id+"F8.opExtrude","SWEPT_FACE",FACE,{"disambiguationData":[OSD([sQuery(id+"F7.wireOp",EDGE,"E67")])]})]});}
            var Q5;
            Q5=makeQuery(id+"F8.boolean.opBoolean","INTERSECT",EDGE,{"disambiguationData":[OD(0.0)],"derivedFrom":[makeQuery(id+"F5.opExtrude","SWEPT_FACE",FACE,{"disambiguationData":[OSD([sQuery(id+"F4.wireOp",EDGE,"E30")])]}),makeQuery(id+"F8.opExtrude","SWEPT_FACE",FACE,{"disambiguationData":[OSD([sQuery(id+"F7.wireOp",EDGE,"E67")])]})]});
            fillet(context, id + "F14", {"entities" : qUnion([Q0, Q1, Q2, Q3, Q4, Q5]), "radius" : 3 * mm, "tangentPropagation" : true, "allowEdgeOverflow" : false});
        }
        {
            var Q0;
            Q0=makeQuery(id+"F1.opExtrude","CAP_EDGE",EDGE,{"disambiguationData":[OSD([sQuery(id+"F0.wireOp",EDGE,"E1.bottom")])],"isStart":false});
            fillet(context, id + "F15", {"entities" : qUnion([Q0]), "radius" : 2 * mm, "tangentPropagation" : true, "allowEdgeOverflow" : false});
        }
        {
            var Q0;
            {var subQ0=sQuery(id+"F0.wireOp",EDGE,"E21.filletArc");var subQ1=sQuery(id+"F0.wireOp",EDGE,"E7");var subQ2=sQuery(id+"F0.wireOp",EDGE,"E6");var subQ3=sQuery(id+"F0.wireOp",EDGE,"E5");var subQ4=sQuery(id+"F0.wireOp",EDGE,"E4");var subQ5=sQuery(id+"F0.wireOp",EDGE,"E22.filletArc");var subQ6=sQuery(id+"F0.wireOp",EDGE,"E1.bottom");var subQ7=sQuery(id+"F0.wireOp",EDGE,"E1.right");var subQ8=sQuery(id+"F0.wireOp",EDGE,"E1.top");var subQ9=sQuery(id+"F0.wireOp",EDGE,"E1.left");var subQ10=sQuery(id+"F0.wireOp",EDGE,"E23.filletArc");var subQ11=sQuery(id+"F0.wireOp",EDGE,"E24.filletArc");Q0=makeQuery(id+"F2.boolean.opBoolean","SPLIT",FACE,{"disambiguationData":[TD([makeQuery(id+"F1.opExtrude","SWEPT_FACE",FACE,{"disambiguationData":[OSD([subQ6])]})])],"derivedFrom":makeQuery(id+"F1.opExtrude","CAP_FACE",FACE,{"disambiguationData":[OSD([subQ6,subQ8,subQ9,subQ7,subQ4,subQ3,subQ2,subQ1,subQ0,subQ5,subQ10,subQ11])],"isStart":true})});}
            var sketch = newSketch(context, id + "F16", { "sketchPlane" : qUnion([Q0])});
            skLineSegment(sketch, "E79", {"start": v(0, 90) * mm, "end": v(0, 120) * mm, "construction": true});
            skCircle(sketch, "E80", {"center": v(0, 120) * mm, "radius": 6 * mm});
            skArc(sketch, "E81", {"start": v(15, 120) * mm, "mid": v(0, 135) * mm, "end": v(-15, 120) * mm});
            skLineSegment(sketch, "E82", {"start": v(-15, 120) * mm, "end": v(-15, 108) * mm});
            skLineSegment(sketch, "E83", {"start": v(-15, 108) * mm, "end": v(-33, 90) * mm});
            skLineSegment(sketch, "E84", {"start": v(15, 120) * mm, "end": v(15, 108) * mm});
            skLineSegment(sketch, "E85", {"start": v(15, 108) * mm, "end": v(33, 90) * mm});
            skLineSegment(sketch, "E86", {"start": v(0, -90) * mm, "end": v(0, -120) * mm, "construction": true});
            skCircle(sketch, "E87", {"center": v(0, -120) * mm, "radius": 6 * mm});
            skArc(sketch, "E88", {"start": v(-15, -120) * mm, "mid": v(0, -135) * mm, "end": v(15, -120) * mm});
            skLineSegment(sketch, "E89", {"start": v(15, -120) * mm, "end": v(15, -108) * mm});
            skLineSegment(sketch, "E90", {"start": v(-15, -120) * mm, "end": v(-15, -108) * mm});
            skLineSegment(sketch, "E91", {"start": v(15, -108) * mm, "end": v(33, -90) * mm});
            skLineSegment(sketch, "E92", {"start": v(-15, -108) * mm, "end": v(-33, -90) * mm});
            skLineSegment(sketch, "E93", {"start": v(-80, 0) * mm, "end": v(80, 0) * mm, "construction": true});
            skSolve(sketch);
        }
        {
            var Q0;
            Q0=makeQuery(id+"F16.imprint","IMPRINT",FACE,{"disambiguationData":[TD([[makeQuery(id+"F16.imprint","IMPRINT",EDGE,{"derivedFrom":sQuery(id+"F16.wireOp",EDGE,"E80")}),-1.0]])]});
            var Q1;
            Q1=makeQuery(id+"F16.imprint","IMPRINT",FACE,{"disambiguationData":[TD([[makeQuery(id+"F16.imprint","IMPRINT",EDGE,{"derivedFrom":makeQuery(id+"F1.opExtrude","CAP_EDGE",EDGE,{"disambiguationData":[OSD([sQuery(id+"F0.wireOp",EDGE,"E1.left")])],"isStart":true})}),-1.0]])]});
            var Q2;
            Q2=makeQuery(id+"F16.imprint","IMPRINT",FACE,{"disambiguationData":[TD([[makeQuery(id+"F16.imprint","IMPRINT",EDGE,{"derivedFrom":sQuery(id+"F16.wireOp",EDGE,"E87")}),-1.0]])]});
            var Q3;
            Q3=makeQuery(id+"F2.opExtrude","CAP_FACE",FACE,{"disambiguationData":[OSD([sQuery(id+"F0.wireOp",EDGE,"E12"),sQuery(id+"F0.wireOp",EDGE,"E13"),sQuery(id+"F0.wireOp",EDGE,"E14"),sQuery(id+"F0.wireOp",EDGE,"E15"),sQuery(id+"F0.wireOp",EDGE,"E17.filletArc"),sQuery(id+"F0.wireOp",EDGE,"E18.filletArc"),sQuery(id+"F0.wireOp",EDGE,"E19.filletArc"),sQuery(id+"F0.wireOp",EDGE,"E20.filletArc"),sQuery(id+"F0.wireOp",EDGE,"E25.0"),sQuery(id+"F0.wireOp",EDGE,"E25.1"),sQuery(id+"F0.wireOp",EDGE,"E25.2"),sQuery(id+"F0.wireOp",EDGE,"E25.3"),sQuery(id+"F0.wireOp",EDGE,"E25.4"),sQuery(id+"F0.wireOp",EDGE,"E25.5"),sQuery(id+"F0.wireOp",EDGE,"E25.6"),sQuery(id+"F0.wireOp",EDGE,"E25.7")])],"isStart":false});
            extrude(context, id + "F17", {"entities" : qUnion([Q0, Q1, Q2]), "endBound" : BoundingType.UP_TO_SURFACE, "depth" : 25 * mm, "endBoundEntityFace" : qUnion([Q3]), "offsetDistance" : 25 * mm});
        }
    });
